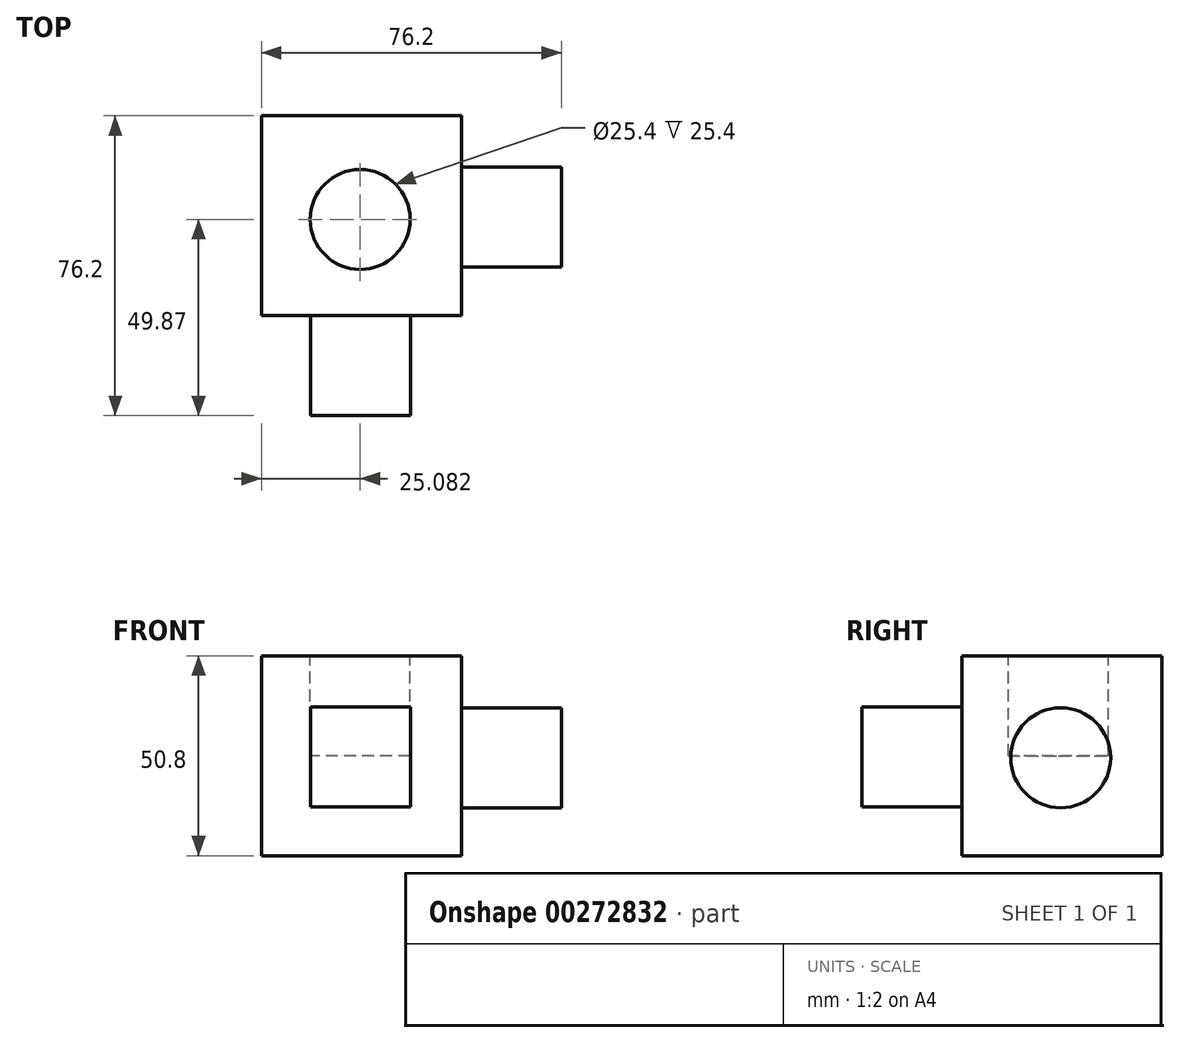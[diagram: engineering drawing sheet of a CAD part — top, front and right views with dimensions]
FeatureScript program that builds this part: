
annotation { "Feature Type Name" : "Feature", "Feature Type Description" : "" }
export const myFeature = defineFeature(function(context is Context, id is Id, definition is map)
    precondition{}
    {
        {
            var Q0;
            Q0=qCreatedBy(makeId("Front.planeOp"),FACE);
            var sketch = newSketch(context, id + "F0", { "sketchPlane" : qUnion([Q0])});
            skLineSegment(sketch, "E0", {"start": v(0, 0) * mm, "end": v(-50.8, 0) * mm});
            skLineSegment(sketch, "E1", {"start": v(-50.8, 0) * mm, "end": v(-50.8, 50.8) * mm});
            skLineSegment(sketch, "E2", {"start": v(-50.8, 50.8) * mm, "end": v(0, 50.8) * mm});
            skLineSegment(sketch, "E3", {"start": v(0, 50.8) * mm, "end": v(0, 0) * mm});
            skSolve(sketch);
        }
        {
            var Q0;
            Q0=makeQuery(id+"F0.imprint","IMPRINT",FACE,{"disambiguationData":[TD([[makeQuery(id+"F0.imprint","IMPRINT",EDGE,{"derivedFrom":sQuery(id+"F0.wireOp",EDGE,"E0")}),-1.0]])]});
            extrude(context, id + "F1", {"entities" : qUnion([Q0]), "depth" : 76.2 * mm});
        }
        {
            var Q0;
            Q0=makeQuery(id+"F1.opExtrude","CAP_FACE",FACE,{"disambiguationData":[OSD([sQuery(id+"F0.wireOp",EDGE,"E0"),sQuery(id+"F0.wireOp",EDGE,"E1"),sQuery(id+"F0.wireOp",EDGE,"E2"),sQuery(id+"F0.wireOp",EDGE,"E3")])],"isStart":false});
            extrude(context, id + "F2", {"entities" : qUnion([Q0]), "operationType" : NewBodyOperationType.REMOVE, "oppositeDirection" : true, "depth" : 25.4 * mm});
        }
        {
            var Q0;
            Q0=makeQuery(id+"F1.opExtrude","SWEPT_FACE",FACE,{"disambiguationData":[OSD([sQuery(id+"F0.wireOp",EDGE,"E2")])]});
            var sketch = newSketch(context, id + "F3", { "sketchPlane" : qUnion([Q0])});
            skCircle(sketch, "E4", {"center": v(-25.72, -26.33) * mm, "radius": 12.7 * mm});
            skSolve(sketch);
        }
        {
            var Q0;
            Q0=makeQuery(id+"F3.imprint","IMPRINT",FACE,{"disambiguationData":[TD([[makeQuery(id+"F3.imprint","IMPRINT",EDGE,{"derivedFrom":sQuery(id+"F3.wireOp",EDGE,"E4")}),1.0]])]});
            extrude(context, id + "F4", {"entities" : qUnion([Q0]), "operationType" : NewBodyOperationType.REMOVE, "oppositeDirection" : true, "depth" : 25.4 * mm});
        }
        {
            var Q0;
            Q0=makeQuery(id+"F2.boolean.opBoolean","COPY",FACE,{"derivedFrom":makeQuery(id+"F2.opExtrude","CAP_FACE",FACE,{"disambiguationData":[OSD([sQuery(id+"F0.wireOp",EDGE,"E0"),sQuery(id+"F0.wireOp",EDGE,"E1"),sQuery(id+"F0.wireOp",EDGE,"E2"),sQuery(id+"F0.wireOp",EDGE,"E3")])],"isStart":false})});
            extrude(context, id + "F5", {"entities" : qUnion([Q0]), "operationType" : NewBodyOperationType.ADD, "depth" : 25.4 * mm});
        }
        {
            var Q0;
            Q0=makeQuery(id+"F5.opExtrude","CAP_FACE",FACE,{"disambiguationData":[OSD([sQuery(id+"F0.wireOp",EDGE,"E0"),sQuery(id+"F0.wireOp",EDGE,"E1"),sQuery(id+"F0.wireOp",EDGE,"E2"),sQuery(id+"F0.wireOp",EDGE,"E3")])],"isStart":false});
            var sketch = newSketch(context, id + "F6", { "sketchPlane" : qUnion([Q0])});
            skLineSegment(sketch, "E5", {"start": v(-38.37, 12.45) * mm, "end": v(-12.97, 12.45) * mm});
            skLineSegment(sketch, "E6", {"start": v(-12.97, 12.45) * mm, "end": v(-12.97, 37.85) * mm});
            skLineSegment(sketch, "E7", {"start": v(-12.97, 37.85) * mm, "end": v(-38.37, 37.85) * mm});
            skLineSegment(sketch, "E8", {"start": v(-38.37, 37.85) * mm, "end": v(-38.37, 12.45) * mm});
            skSolve(sketch);
        }
        {
            var Q0;
            Q0=makeQuery(id+"F6.imprint","IMPRINT",FACE,{"disambiguationData":[TD([[makeQuery(id+"F6.imprint","IMPRINT",EDGE,{"derivedFrom":sQuery(id+"F6.wireOp",EDGE,"E5")}),1.0]])]});
            extrude(context, id + "F7", {"entities" : qUnion([Q0]), "operationType" : NewBodyOperationType.ADD, "depth" : 25.4 * mm});
        }
        {
            var Q0;
            Q0=makeQuery(id+"F5.opExtrude","CAP_FACE",FACE,{"disambiguationData":[OSD([sQuery(id+"F0.wireOp",EDGE,"E0"),sQuery(id+"F0.wireOp",EDGE,"E1"),sQuery(id+"F0.wireOp",EDGE,"E2"),sQuery(id+"F0.wireOp",EDGE,"E3")])],"isStart":false});
            extrude(context, id + "F8", {"entities" : qUnion([Q0]), "operationType" : NewBodyOperationType.REMOVE, "oppositeDirection" : true, "depth" : 25.4 * mm});
        }
        {
            var Q0;
            Q0=makeQuery(id+"F7.opExtrude","CAP_FACE",FACE,{"disambiguationData":[OSD([sQuery(id+"F6.wireOp",EDGE,"E5"),sQuery(id+"F6.wireOp",EDGE,"E6"),sQuery(id+"F6.wireOp",EDGE,"E7"),sQuery(id+"F6.wireOp",EDGE,"E8")])],"isStart":false});
            extrude(context, id + "F9", {"entities" : qUnion([Q0]), "operationType" : NewBodyOperationType.REMOVE, "oppositeDirection" : true, "depth" : 25.4 * mm});
        }
        {
            var Q0;
            {var subQ0=sQuery(id+"F0.wireOp",EDGE,"E3");Q0=makeQuery(id+"F5.boolean.opBoolean","MERGE",FACE,{"derivedFrom":[makeQuery(id+"F1.opExtrude","SWEPT_FACE",FACE,{"disambiguationData":[OSD([subQ0])]}),makeQuery(id+"F5.opExtrude","SWEPT_FACE",FACE,{"disambiguationData":[OSD([subQ0])]})]});}
            var sketch = newSketch(context, id + "F10", { "sketchPlane" : qUnion([Q0])});
            skCircle(sketch, "E9", {"center": v(-25.72, 24.9) * mm, "radius": 12.7 * mm});
            skSolve(sketch);
        }
        {
            var Q0;
            Q0=makeQuery(id+"F10.imprint","IMPRINT",FACE,{"disambiguationData":[TD([[makeQuery(id+"F10.imprint","IMPRINT",EDGE,{"derivedFrom":sQuery(id+"F10.wireOp",EDGE,"E9")}),1.0]])]});
            extrude(context, id + "F11", {"entities" : qUnion([Q0]), "operationType" : NewBodyOperationType.ADD, "depth" : 25.4 * mm});
        }
    });
